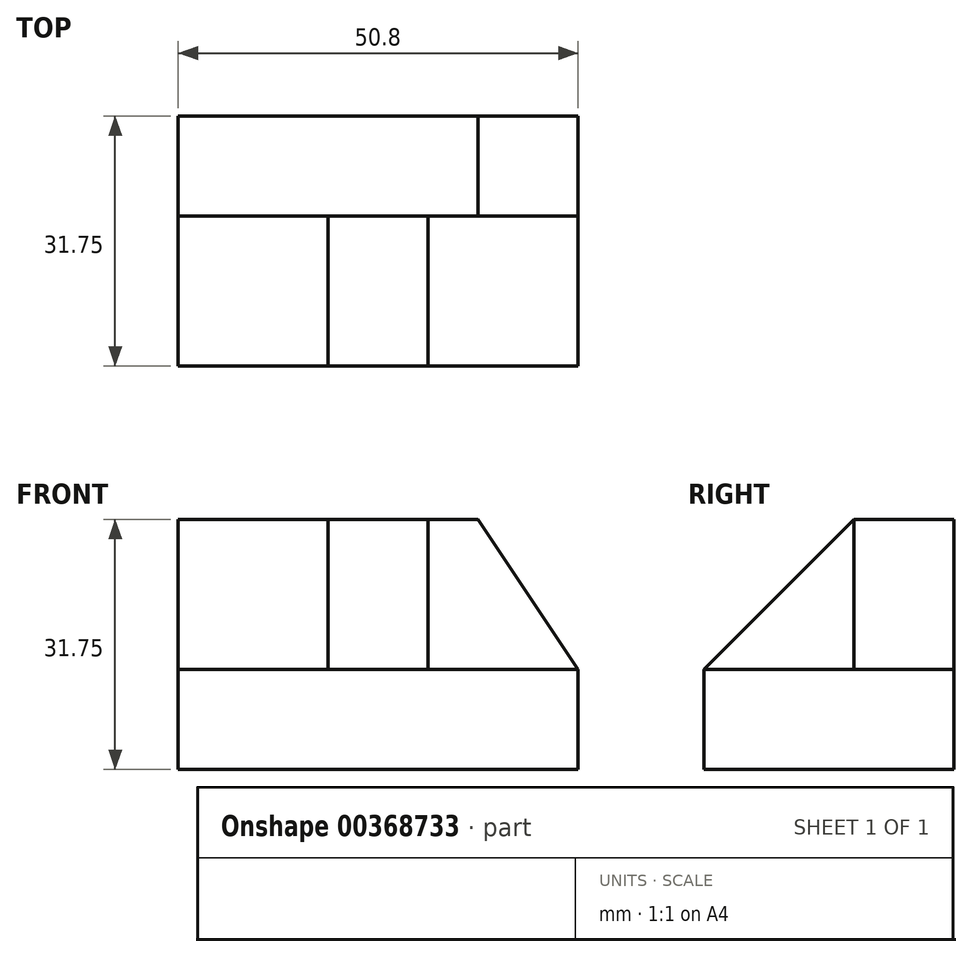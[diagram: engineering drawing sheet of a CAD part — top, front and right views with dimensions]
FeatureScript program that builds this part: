
annotation { "Feature Type Name" : "Feature", "Feature Type Description" : "" }
export const myFeature = defineFeature(function(context is Context, id is Id, definition is map)
    precondition{}
    {
        {
            var Q0;
            Q0=qCreatedBy(makeId("Top.planeOp"),FACE);
            var sketch = newSketch(context, id + "F0", { "sketchPlane" : qUnion([Q0])});
            skLineSegment(sketch, "E0", {"start": v(0, 0) * mm, "end": v(0, 31.75) * mm});
            skLineSegment(sketch, "E1", {"start": v(0, 31.75) * mm, "end": v(50.8, 31.75) * mm});
            skLineSegment(sketch, "E2", {"start": v(50.8, 31.75) * mm, "end": v(50.8, 0) * mm});
            skLineSegment(sketch, "E3", {"start": v(50.8, 0) * mm, "end": v(0, 0) * mm});
            skSolve(sketch);
        }
        {
            var Q0;
            Q0=makeQuery(id+"F0.imprint","IMPRINT",FACE,{"disambiguationData":[TD([[makeQuery(id+"F0.imprint","IMPRINT",EDGE,{"derivedFrom":sQuery(id+"F0.wireOp",EDGE,"E0")}),-1.0]])]});
            extrude(context, id + "F1", {"entities" : qUnion([Q0]), "depth" : 12.7 * mm});
        }
        {
            var Q0;
            Q0=makeQuery(id+"F1.opExtrude","SWEPT_FACE",FACE,{"disambiguationData":[OSD([sQuery(id+"F0.wireOp",EDGE,"E2")])]});
            var sketch = newSketch(context, id + "F2", { "sketchPlane" : qUnion([Q0])});
            skLineSegment(sketch, "E4", {"start": v(19.05, 12.7) * mm, "end": v(31.75, 12.7) * mm});
            skLineSegment(sketch, "E5", {"start": v(31.75, 12.7) * mm, "end": v(31.75, 31.75) * mm});
            skLineSegment(sketch, "E6", {"start": v(31.75, 31.75) * mm, "end": v(19.05, 31.75) * mm});
            skLineSegment(sketch, "E7", {"start": v(19.05, 31.75) * mm, "end": v(19.05, 12.7) * mm});
            skSolve(sketch);
        }
        {
            var Q0;
            Q0=makeQuery(id+"F2.imprint","IMPRINT",FACE,{"disambiguationData":[TD([[makeQuery(id+"F2.imprint","IMPRINT",EDGE,{"derivedFrom":sQuery(id+"F2.wireOp",EDGE,"E4")}),-1.0]])]});
            extrude(context, id + "F3", {"entities" : qUnion([Q0]), "operationType" : NewBodyOperationType.ADD, "oppositeDirection" : true, "depth" : 50.8 * mm});
        }
        {
            var Q0;
            Q0=makeQuery(id+"F3.opExtrude","SWEPT_FACE",FACE,{"disambiguationData":[OSD([sQuery(id+"F2.wireOp",EDGE,"E7")])]});
            var sketch = newSketch(context, id + "F4", { "sketchPlane" : qUnion([Q0])});
            skLineSegment(sketch, "E8", {"start": v(38.1, 31.75) * mm, "end": v(50.8, 31.75) * mm});
            skLineSegment(sketch, "E9", {"start": v(50.8, 31.75) * mm, "end": v(50.8, 12.7) * mm});
            skLineSegment(sketch, "E10", {"start": v(50.8, 12.7) * mm, "end": v(38.1, 31.75) * mm});
            skSolve(sketch);
        }
        {
            var Q0;
            Q0=makeQuery(id+"F4.imprint","IMPRINT",FACE,{"disambiguationData":[TD([[makeQuery(id+"F4.imprint","IMPRINT",EDGE,{"derivedFrom":sQuery(id+"F4.wireOp",EDGE,"E8")}),-1.0]])]});
            extrude(context, id + "F5", {"entities" : qUnion([Q0]), "operationType" : NewBodyOperationType.REMOVE, "oppositeDirection" : true, "depth" : 12.7 * mm});
        }
        {
            var Q0;
            Q0=makeQuery(id+"F3.opExtrude","SWEPT_FACE",FACE,{"disambiguationData":[OSD([sQuery(id+"F2.wireOp",EDGE,"E7")])]});
            var sketch = newSketch(context, id + "F6", { "sketchPlane" : qUnion([Q0])});
            skLineSegment(sketch, "E11", {"start": v(0, 31.75) * mm, "end": v(19.05, 31.75) * mm});
            skLineSegment(sketch, "E12", {"start": v(19.05, 31.75) * mm, "end": v(19.05, 12.7) * mm});
            skLineSegment(sketch, "E13", {"start": v(19.05, 12.7) * mm, "end": v(31.75, 12.7) * mm});
            skLineSegment(sketch, "E14", {"start": v(31.75, 12.7) * mm, "end": v(31.75, 31.75) * mm});
            skLineSegment(sketch, "E15", {"start": v(31.75, 31.75) * mm, "end": v(19.05, 31.75) * mm});
            skSolve(sketch);
        }
        {
            var Q0;
            Q0=makeQuery(id+"F6.imprint","IMPRINT",FACE,{"disambiguationData":[TD([[makeQuery(id+"F6.imprint","IMPRINT",EDGE,{"derivedFrom":sQuery(id+"F6.wireOp",EDGE,"E12")}),1.0]])]});
            extrude(context, id + "F7", {"entities" : qUnion([Q0]), "operationType" : NewBodyOperationType.ADD, "depth" : 19.05 * mm});
        }
        {
            var Q0;
            Q0=makeQuery(id+"F7.opExtrude","SWEPT_FACE",FACE,{"disambiguationData":[OSD([sQuery(id+"F6.wireOp",EDGE,"E14")])]});
            var sketch = newSketch(context, id + "F8", { "sketchPlane" : qUnion([Q0])});
            skLineSegment(sketch, "E16", {"start": v(19.05, 31.75) * mm, "end": v(0, 12.7) * mm});
            skLineSegment(sketch, "E17", {"start": v(0, 12.7) * mm, "end": v(0, 31.75) * mm});
            skLineSegment(sketch, "E18", {"start": v(0, 31.75) * mm, "end": v(19.05, 31.75) * mm});
            skSolve(sketch);
        }
        {
            var Q0;
            Q0=makeQuery(id+"F8.imprint","IMPRINT",FACE,{"disambiguationData":[TD([[makeQuery(id+"F8.imprint","IMPRINT",EDGE,{"derivedFrom":sQuery(id+"F8.wireOp",EDGE,"E16")}),-1.0]])]});
            extrude(context, id + "F9", {"entities" : qUnion([Q0]), "operationType" : NewBodyOperationType.REMOVE, "oppositeDirection" : true, "depth" : 12.7 * mm});
        }
    });
